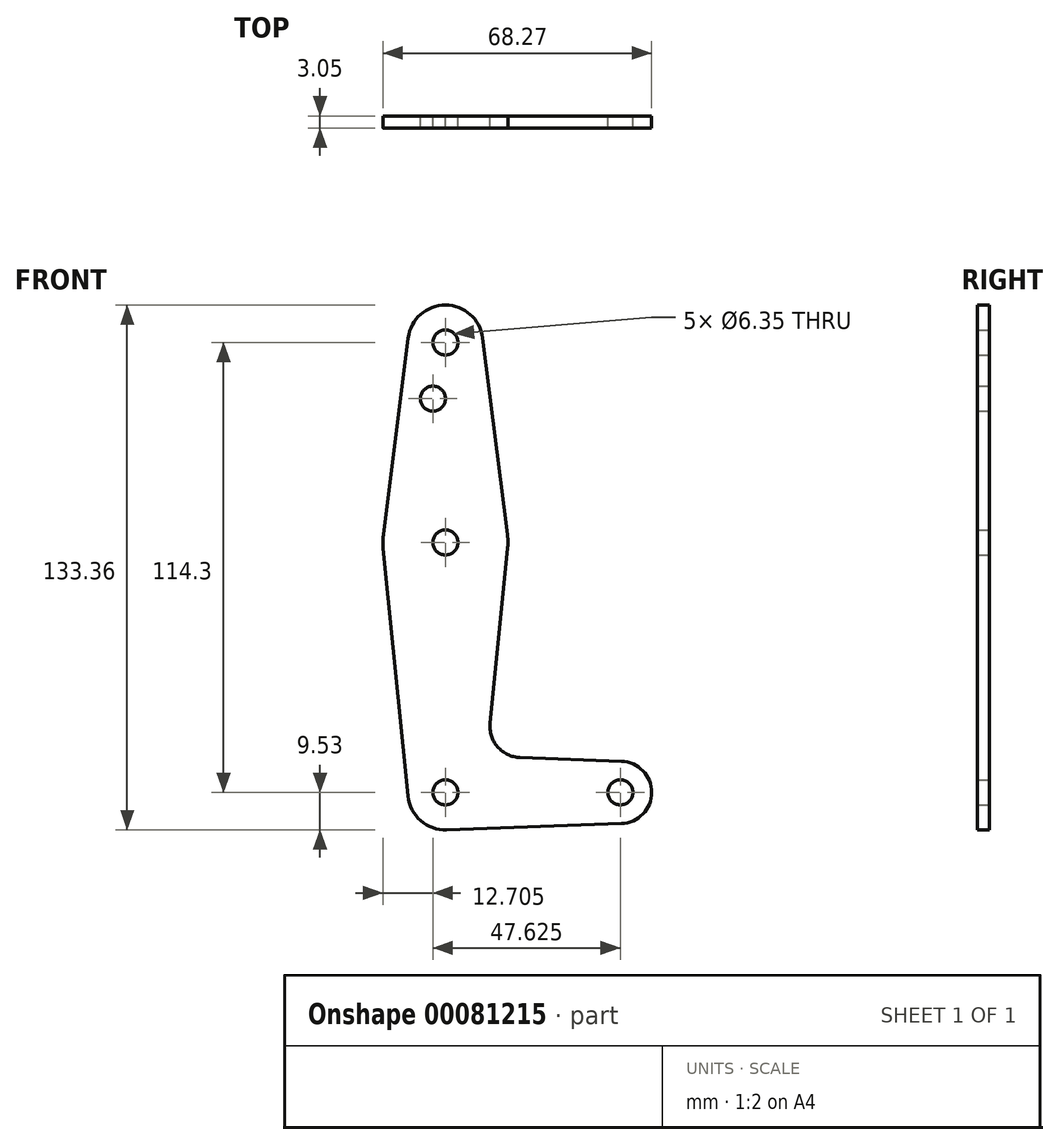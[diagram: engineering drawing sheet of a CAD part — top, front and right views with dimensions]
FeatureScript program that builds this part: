
annotation { "Feature Type Name" : "Feature", "Feature Type Description" : "" }
export const myFeature = defineFeature(function(context is Context, id is Id, definition is map)
    precondition{}
    {
        {
            var Q0;
            Q0=qCreatedBy(makeId("Front.planeOp"),FACE);
            var sketch = newSketch(context, id + "F0", { "sketchPlane" : qUnion([Q0])});
            skLineSegment(sketch, "E0", {"start": v(0, 0) * mm, "end": v(0, -114.3) * mm, "construction": true});
            skLineSegment(sketch, "E1", {"start": v(0, -114.3) * mm, "end": v(44.45, -114.3) * mm, "construction": true});
            skCircle(sketch, "E2", {"center": v(0, 0) * mm, "radius": 9.53 * mm});
            skCircle(sketch, "E3", {"center": v(44.45, -114.3) * mm, "radius": 7.94 * mm});
            skCircle(sketch, "E4", {"center": v(0, -114.3) * mm, "radius": 9.53 * mm});
            skCircle(sketch, "E5", {"center": v(0, -50.8) * mm, "radius": 15.88 * mm});
            skLineSegment(sketch, "E6", {"start": v(9.45, 1.2) * mm, "end": v(15.75, -48.82) * mm});
            skLineSegment(sketch, "E7", {"start": v(15.8, -52.39) * mm, "end": v(11.34, -96.7) * mm});
            skLineSegment(sketch, "E8", {"start": v(-15.8, -52.39) * mm, "end": v(-9.48, -115.25) * mm});
            skLineSegment(sketch, "E9", {"start": v(-9.45, 1.2) * mm, "end": v(-15.75, -48.82) * mm});
            skLineSegment(sketch, "E10", {"start": v(18.97, -105.45) * mm, "end": v(44.73, -106.37) * mm});
            skLineSegment(sketch, "E11", {"start": v(0.34, -123.82) * mm, "end": v(44.73, -122.23) * mm});
            skCircle(sketch, "E12", {"center": v(0, 0) * mm, "radius": 3.18 * mm});
            skCircle(sketch, "E13", {"center": v(0, -50.8) * mm, "radius": 3.18 * mm});
            skCircle(sketch, "E14", {"center": v(0, -114.3) * mm, "radius": 3.18 * mm});
            skCircle(sketch, "E15", {"center": v(44.45, -114.3) * mm, "radius": 3.18 * mm});
            skCircle(sketch, "E16", {"center": v(-3.18, -14.27) * mm, "radius": 3.18 * mm});
            skArc(sketch, "E17.filletArc", {"start": v(11.34, -96.7) * mm, "mid": v(13.26, -102.73) * mm, "end": v(18.97, -105.45) * mm});
            skSolve(sketch);
        }
        {
            var Q0;
            Q0 = qSketchRegion(id + "F0", true);
            extrude(context, id + "F1", {"entities" : qUnion([Q0]), "depth" : 3.05 * mm});
        }
    });
